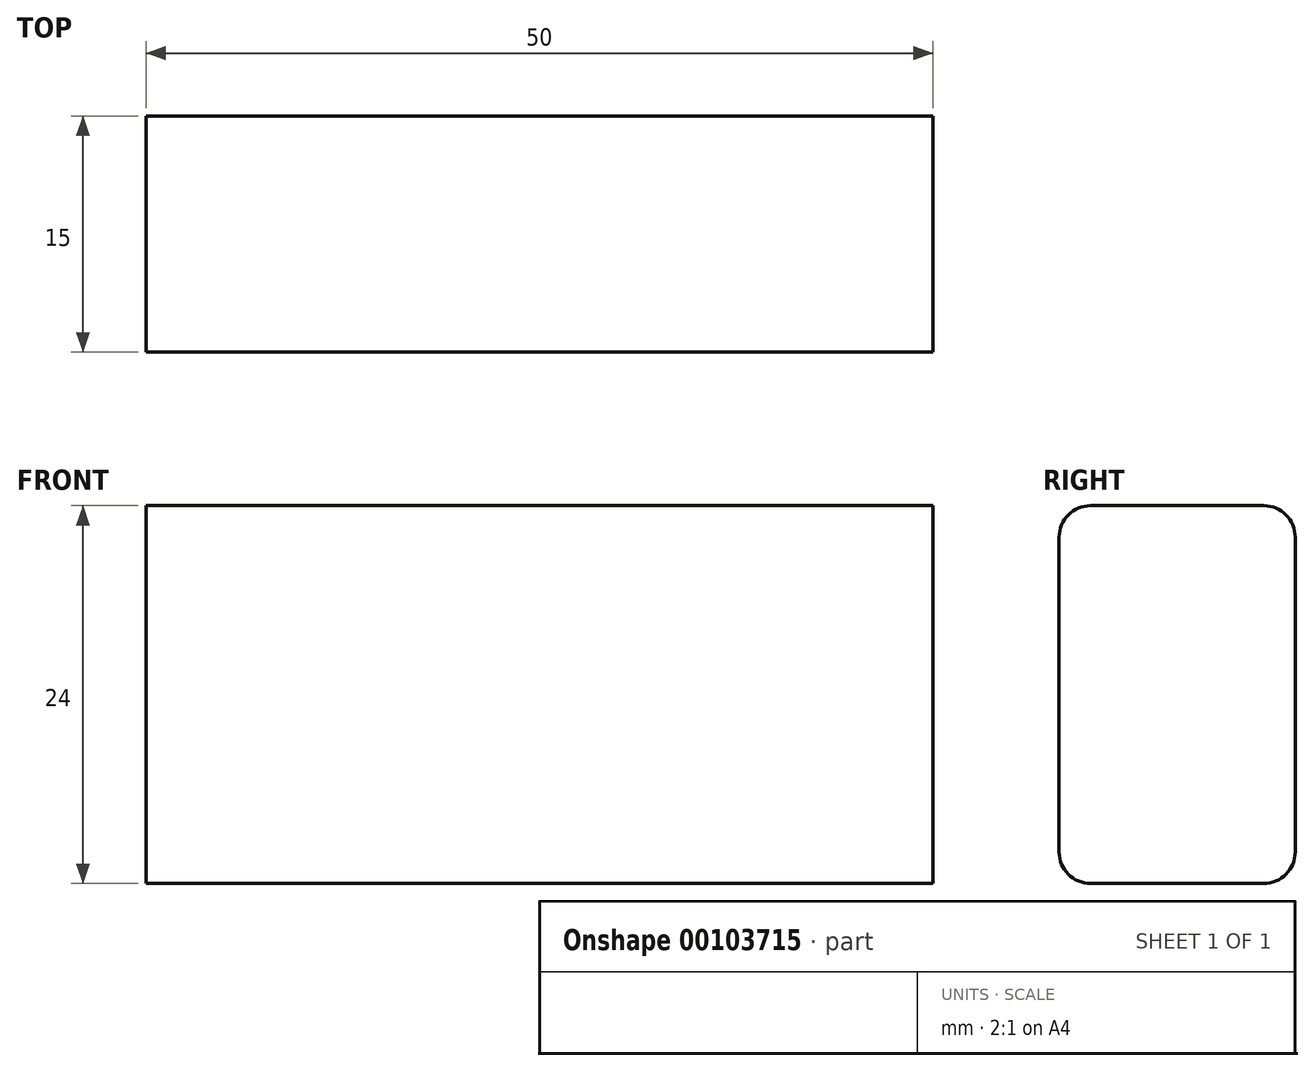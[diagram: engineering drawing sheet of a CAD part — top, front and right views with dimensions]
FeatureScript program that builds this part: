
annotation { "Feature Type Name" : "Feature", "Feature Type Description" : "" }
export const myFeature = defineFeature(function(context is Context, id is Id, definition is map)
    precondition{}
    {
        {
            var Q0;
            Q0=qCreatedBy(makeId("Front.planeOp"),FACE);
            var sketch = newSketch(context, id + "F0", { "sketchPlane" : qUnion([Q0])});
            skLineSegment(sketch, "E0.bottom", {"start": v(-25, 12) * mm, "end": v(25, 12) * mm});
            skLineSegment(sketch, "E0.top", {"start": v(-25, -12) * mm, "end": v(25, -12) * mm});
            skLineSegment(sketch, "E0.left", {"start": v(-25, 12) * mm, "end": v(-25, -12) * mm});
            skLineSegment(sketch, "E0.right", {"start": v(25, 12) * mm, "end": v(25, -12) * mm});
            skPoint(sketch, "E0.middle", {"position": v(0, 0) * mm});
            skSolve(sketch);
        }
        {
            var Q0;
            Q0=makeQuery(id+"F0.imprint","IMPRINT",FACE,{"disambiguationData":[TD([[makeQuery(id+"F0.imprint","IMPRINT",EDGE,{"derivedFrom":sQuery(id+"F0.wireOp",EDGE,"E0.bottom")}),-1.0]])]});
            extrude(context, id + "F1", {"entities" : qUnion([Q0]), "depth" : 15 * mm});
        }
        {
            var Q0;
            Q0=makeQuery(id+"F1.opExtrude","CAP_EDGE",EDGE,{"disambiguationData":[OSD([sQuery(id+"F0.wireOp",EDGE,"E0.bottom")])],"isStart":false});
            fillet(context, id + "F2", {"entities" : qUnion([Q0]), "radius" : 2 * mm, "tangentPropagation" : true, "allowEdgeOverflow" : false});
        }
        {
            var Q0;
            Q0=makeQuery(id+"F1.opExtrude","CAP_EDGE",EDGE,{"disambiguationData":[OSD([sQuery(id+"F0.wireOp",EDGE,"E0.bottom")])],"isStart":true});
            var Q1;
            Q1=makeQuery(id+"F1.opExtrude","CAP_EDGE",EDGE,{"disambiguationData":[OSD([sQuery(id+"F0.wireOp",EDGE,"E0.top")])],"isStart":false});
            fillet(context, id + "F3", {"entities" : qUnion([Q0, Q1]), "radius" : 2 * mm, "tangentPropagation" : true, "allowEdgeOverflow" : false});
        }
        {
            var Q0;
            Q0=makeQuery(id+"F1.opExtrude","CAP_EDGE",EDGE,{"disambiguationData":[OSD([sQuery(id+"F0.wireOp",EDGE,"E0.top")])],"isStart":true});
            fillet(context, id + "F4", {"entities" : qUnion([Q0]), "radius" : 2 * mm, "tangentPropagation" : true, "allowEdgeOverflow" : false});
        }
        {
            var Q0;
            Q0=makeQuery(id+"F1.opExtrude","SWEPT_FACE",FACE,{"disambiguationData":[OSD([sQuery(id+"F0.wireOp",EDGE,"E0.right")])]});
            var sketch = newSketch(context, id + "F5", { "sketchPlane" : qUnion([Q0])});
            skCircle(sketch, "E1", {"center": v(-7.5, 6) * mm, "radius": 3 * mm});
            skSolve(sketch);
        }
        {
            var Q0;
            Q0=makeQuery(id+"F5.imprint","IMPRINT",FACE,{"disambiguationData":[TD([[makeQuery(id+"F5.imprint","IMPRINT",EDGE,{"derivedFrom":sQuery(id+"F5.wireOp",EDGE,"E1")}),-1.0]])]});
            var sketch = newSketch(context, id + "F6", { "sketchPlane" : qUnion([Q0])});
            skCircle(sketch, "E2", {"center": v(-7.5, -6) * mm, "radius": 3 * mm});
            skSolve(sketch);
        }
        {
            var Q0;
            Q0=sQuery(id+"F5.wireOp",EDGE,"E1");
            var Q1;
            Q1=sQuery(id+"F6.wireOp",EDGE,"E2");
            extrude(context, id + "F7", {"bodyType" : ToolBodyType.SURFACE, "operationType" : NewBodyOperationType.ADD, "surfaceEntities" : qUnion([Q0, Q1]), "depth" : 4 * mm});
        }
    });
